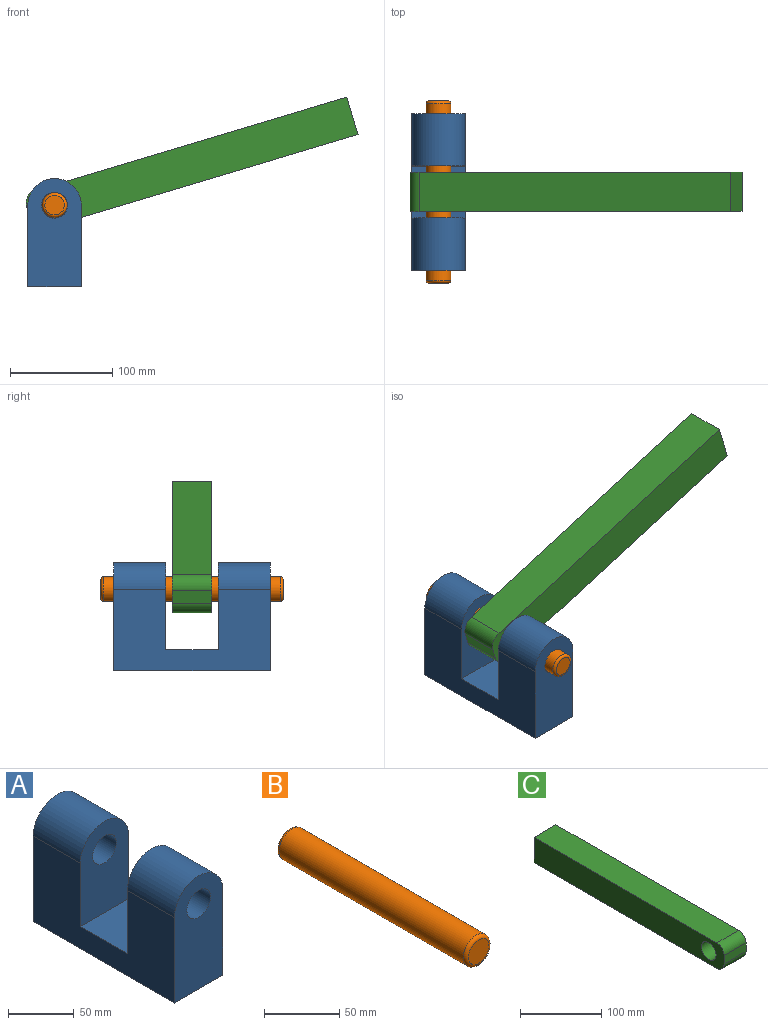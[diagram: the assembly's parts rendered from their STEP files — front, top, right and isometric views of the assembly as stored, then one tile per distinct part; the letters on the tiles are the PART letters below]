
ASSEMBLY  parts=3 mates=2
PART A: 12 faces, bbox 52.1x152.4x105.8 mm
  f0: plane 152.4x79.68mm, normal (1,0,0), area 9143.9mm2, adj f1,f2,f6,f7,f8,f9,f10,f11
  f1: cylinder r=26.07mm len=52.14mm, axis (0,1,0), area 4160.6mm2, adj f0,f3,f7,f10
  f2: cylinder r=26.07mm len=52.14mm, axis (0,1,0), area 4160.6mm2, adj f0,f3,f8,f11
  f3: plane 152.4x79.68mm, normal (-1,0,0), area 9143.9mm2, adj f1,f2,f6,f7,f8,f9,f10,f11
  f4: cylinder r=12.7mm len=50.8mm, axis (0,1,0), area 4053.7mm2, adj f7,f10
  f5: cylinder r=12.7mm len=50.8mm, axis (0,1,0), area 4053.7mm2, adj f8,f11
  f6: plane 152.4x52.14mm, normal (0,0,-1), area 7946.1mm2, adj f0,f3,f7,f8
  f7: plane 105.75x52.14mm, normal (0,-1,0), area 4715.4mm2, adj f0,f1,f3,f4,f6
  f8: plane 105.75x52.14mm, normal (0,1,0), area 4715.4mm2, adj f0,f2,f3,f5,f6
  f9: plane 52.14x50.8mm, normal (0,0,1), area 2648.7mm2, adj f0,f3,f10,f11
  f10: plane 85.12x52.14mm, normal (0,1,0), area 3639.5mm2, adj f0,f1,f3,f4,f9
  f11: plane 85.12x52.14mm, normal (0,-1,0), area 3639.5mm2, adj f0,f2,f3,f5,f9
PART B: 5 faces, bbox 26.1x177.8x26.1 mm
  f0: cylinder r=12.06mm len=172.72mm, axis (0,1,0), area 13093.3mm2, adj f3,f4
  f1: plane 19.05x19.05mm, normal (0,-1,0), area 285mm2, adj f4
  f2: plane 19.05x19.05mm, normal (0,1,0), area 285mm2, adj f3
  f3: torus R=9.53mm, axis (0,-1,0), area 279.3mm2, adj f0,f2
  f4: torus R=9.53mm, axis (0,-1,0), area 279.3mm2, adj f0,f1
PART C: 9 faces, bbox 38.1x330.2x38.1 mm
  f0: plane 317.5x38.1mm, normal (0,0,1), area 12096.7mm2, adj f1,f3,f5,f8
  f1: plane 330.2x38.1mm, normal (-1,0,0), area 12004.7mm2, adj f0,f2,f4,f5,f6,f7,f8
  f2: plane 317.5x38.1mm, normal (0,0,-1), area 12096.7mm2, adj f1,f3,f5,f7
  f3: plane 330.2x38.1mm, normal (1,0,0), area 12004.7mm2, adj f0,f2,f4,f5,f6,f7,f8
  f4: plane 38.1x12.7mm, normal (0,-1,0), area 483.9mm2, adj f1,f3,f7,f8
  f5: plane 38.1x38.1mm, normal (0,1,0), area 1451.6mm2, adj f0,f1,f2,f3
  f6: cylinder r=12.7mm len=38.1mm, axis (1,0,0), area 3040.2mm2, adj f1,f3
  f7: cylinder r=12.7mm len=38.1mm, axis (-1,0,0), area 760.1mm2, adj f1,f2,f3,f4
  f8: cylinder r=12.7mm len=38.1mm, axis (1,0,0), area 760.1mm2, adj f0,f1,f3,f4
PLACE A t=(-105.26,39.4,26.5)mm fixed
PLACE B rot(axis=(0,-1,0),166.1deg) t=(-127.61,52.1,65.86)mm
PLACE C rot(axis=(0.14,-0.14,-0.98),91.2deg) t=(164.09,-40.48,149.89)mm
MATE revolute B.f0 <-> A.f1  axis (0,1,0) through (-127.61,-36.8,65.86)mm
MATE revolute C.f6 <-> B.f0  axis (0,-1,0) through (-127.61,-36.8,65.86)mm
